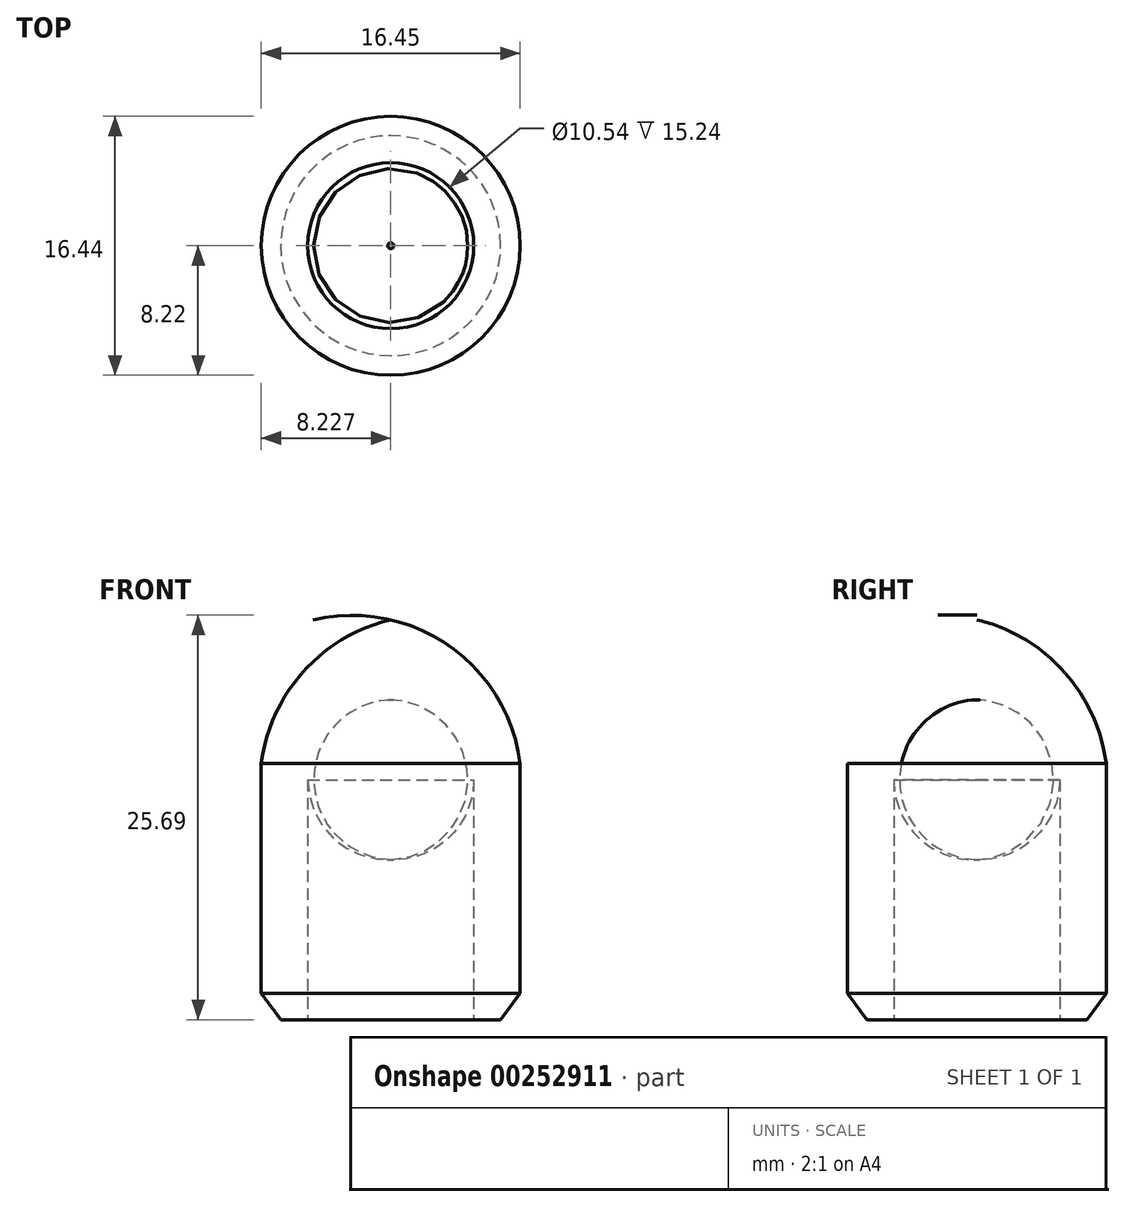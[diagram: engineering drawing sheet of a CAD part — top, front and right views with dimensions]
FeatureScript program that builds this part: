
annotation { "Feature Type Name" : "Feature", "Feature Type Description" : "" }
export const myFeature = defineFeature(function(context is Context, id is Id, definition is map)
    precondition{}
    {
        {
            var Q0;
            Q0=qCreatedBy(makeId("Front.planeOp"),FACE);
            var sketch = newSketch(context, id + "F0", { "sketchPlane" : qUnion([Q0])});
            skLineSegment(sketch, "E0", {"start": v(-0.66, -5.29) * mm, "end": v(6.32, -5.29) * mm});
            skLineSegment(sketch, "E1", {"start": v(6.32, -5.29) * mm, "end": v(7.56, -3.63) * mm});
            skLineSegment(sketch, "E2", {"start": v(-0.66, -5.29) * mm, "end": v(-0.66, 20.11) * mm});
            skLineSegment(sketch, "E3", {"start": v(7.56, -3.63) * mm, "end": v(7.56, 10.97) * mm});
            skArc(sketch, "E4", {"start": v(7.56, 10.97) * mm, "mid": v(4.88, 16.83) * mm, "end": v(-0.66, 20.11) * mm});
            skSolve(sketch);
        }
        {
            var Q0;
            Q0=makeQuery(id+"F0.imprint","IMPRINT",FACE,{"disambiguationData":[TD([[makeQuery(id+"F0.imprint","IMPRINT",EDGE,{"derivedFrom":sQuery(id+"F0.wireOp",EDGE,"E0")}),1.0]])]});
            var Q1;
            Q1=sQuery(id+"F0.wireOp",EDGE,"E2");
            revolve(context, id + "F1", {"entities" : qUnion([Q0]), "axis" : qUnion([Q1]), "revolveType" : RevolveType.FULL});
        }
        {
            var Q0;
            Q0=makeQuery(id+"F1.opRevolve","SWEPT_FACE",FACE,{"disambiguationData":[OSD([sQuery(id+"F0.wireOp",EDGE,"E0")])]});
            var sketch = newSketch(context, id + "F2", { "sketchPlane" : qUnion([Q0])});
            skCircle(sketch, "E5.0.0", {"center": v(-0.66, 0) * mm, "radius": 6.99 * mm});
            skCircle(sketch, "E6", {"center": v(-0.66, 0) * mm, "radius": 5.27 * mm});
            skSolve(sketch);
        }
        {
            var Q0;
            Q0=makeQuery(id+"F2.imprint","IMPRINT",FACE,{"disambiguationData":[TD([[makeQuery(id+"F2.imprint","IMPRINT",EDGE,{"derivedFrom":sQuery(id+"F2.wireOp",EDGE,"E6")}),1.0]])]});
            extrude(context, id + "F3", {"entities" : qUnion([Q0]), "operationType" : NewBodyOperationType.REMOVE, "oppositeDirection" : true, "depth" : 20.32 * mm});
        }
        {
            var Q0;
            Q0=makeQuery(id+"F3.boolean.opBoolean","COPY",EDGE,{"derivedFrom":makeQuery(id+"F3.opExtrude","CAP_EDGE",EDGE,{"disambiguationData":[OSD([sQuery(id+"F2.wireOp",EDGE,"E6")])],"isStart":false})});
            fillet(context, id + "F4", {"entities" : qUnion([Q0]), "radius" : 5.08 * mm, "tangentPropagation" : true, "allowEdgeOverflow" : false});
        }
    });
